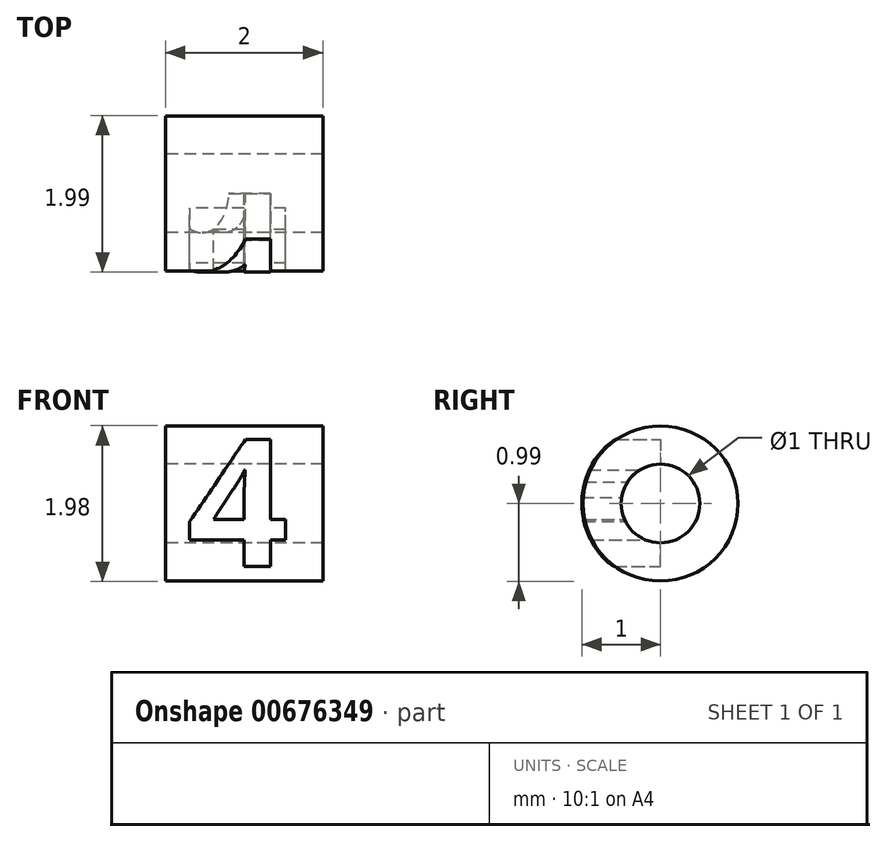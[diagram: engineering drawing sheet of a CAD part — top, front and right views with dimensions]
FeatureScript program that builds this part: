
annotation { "Feature Type Name" : "Feature", "Feature Type Description" : "" }
export const myFeature = defineFeature(function(context is Context, id is Id, definition is map)
    precondition{}
    {
        {
            var Q0;
            Q0=qCreatedBy(makeId("Right.planeOp"),FACE);
            var sketch = newSketch(context, id + "F0", { "sketchPlane" : qUnion([Q0])});
            skCircle(sketch, "E0", {"center": v(0, 0) * mm, "radius": 0.5 * mm});
            skCircle(sketch, "E1", {"center": v(0, 0) * mm, "radius": 1 * mm});
            skCircle(sketch, "E2", {"center": v(0, 0) * mm, "radius": 0.98 * mm});
            skSolve(sketch);
        }
        {
            var Q0;
            Q0=makeQuery(id+"F0.imprint","IMPRINT",FACE,{"disambiguationData":[TD([[makeQuery(id+"F0.imprint","IMPRINT",EDGE,{"derivedFrom":sQuery(id+"F0.wireOp",EDGE,"E0")}),-1.0]])]});
            var Q1;
            Q1=makeQuery(id+"F0.imprint","IMPRINT",FACE,{"disambiguationData":[TD([[makeQuery(id+"F0.imprint","IMPRINT",EDGE,{"derivedFrom":sQuery(id+"F0.wireOp",EDGE,"E1")}),1.0]])]});
            extrude(context, id + "F1", {"entities" : qUnion([Q0, Q1]), "depth" : 2 * mm, "offsetDistance" : 25 * mm});
        }
        {
            var Q0;
            Q0=qCreatedBy(makeId("Front.planeOp"),FACE);
            var sketch = newSketch(context, id + "F2", { "sketchPlane" : qUnion([Q0])});
            skText(sketch, "E3", { "text": "4", "fontName": "OpenSans-Bold.ttf"});
            const initialGuessF2  = {"E3": [0.00027, -0.0008, 1, 0, 0.00163]};
            skSetInitialGuess(sketch, initialGuessF2);
            skSolve(sketch);
        }
        {
            var Q0;
            Q0=qSketchRegion(id+"F2",true);
            var Q1;
            Q1=qConstructionFilter(qBodyType(qCreatedBy(id+"F2",EDGE),BodyType.WIRE),ConstructionObject.NO);
            var Q2;
            Q2=makeQuery(id+"F1.opExtrude","SWEPT_FACE",FACE,{"disambiguationData":[OSD([sQuery(id+"F0.wireOp",EDGE,"E1")])]});
            var Q3;
            Q3=makeQuery(id+"F1.opExtrude","SWEPT_BODY",BODY,{"disambiguationData":[OSD([sQuery(id+"F0.wireOp",EDGE,"E0"),sQuery(id+"F0.wireOp",EDGE,"E1")])]});
            var Q4;
            Q4=sQuery(id+"F0.wireOp",VERTEX,"27635d6e-dcd6-4653-b727-4819003c0945");
            extrude(context, id + "F3", {"entities" : qUnion([Q0]), "operationType" : NewBodyOperationType.INTERSECT, "surfaceEntities" : qUnion([Q1]), "endBound" : BoundingType.UP_TO_SURFACE, "endBoundEntityFace" : qUnion([Q2]), "endBoundEntityBody" : qUnion([Q3]), "endBoundEntityVertex" : qUnion([Q4]), "depth" : 25 * mm, "offsetDistance" : 25 * mm});
        }
        {
            var Q0;
            Q0=makeQuery(id+"F0.imprint","IMPRINT",FACE,{"disambiguationData":[TD([[makeQuery(id+"F0.imprint","IMPRINT",EDGE,{"derivedFrom":sQuery(id+"F0.wireOp",EDGE,"E0")}),-1.0]])]});
            extrude(context, id + "F4", {"entities" : qUnion([Q0]), "depth" : 2 * mm, "offsetDistance" : 25 * mm});
        }
    });
